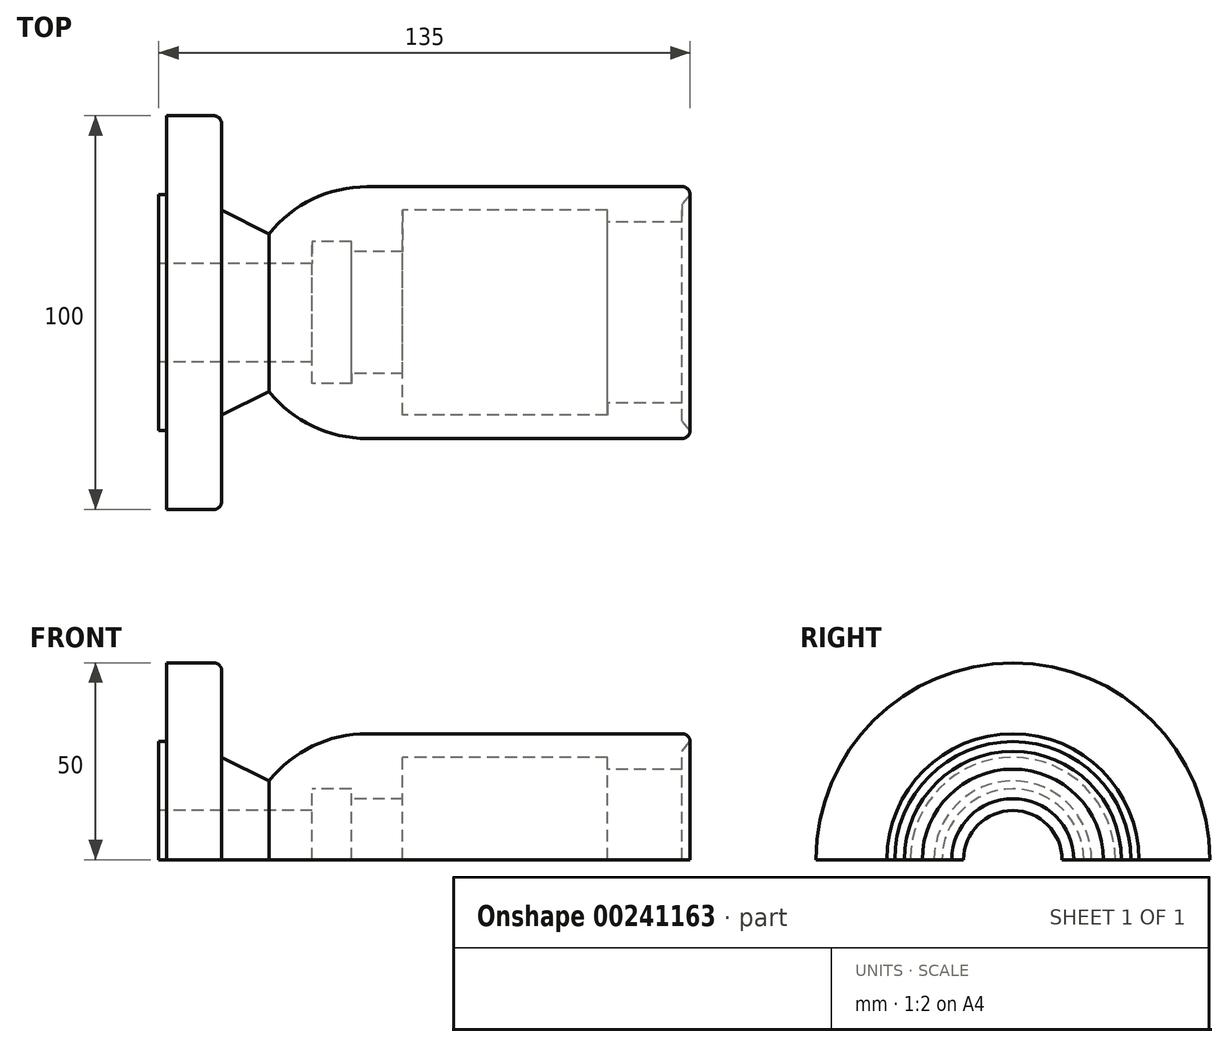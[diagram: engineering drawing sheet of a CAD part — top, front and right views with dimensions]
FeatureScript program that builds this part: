
annotation { "Feature Type Name" : "Feature", "Feature Type Description" : "" }
export const myFeature = defineFeature(function(context is Context, id is Id, definition is map)
    precondition{}
    {
        {
            var Q0;
            Q0=qCreatedBy(makeId("Front.planeOp"),FACE);
            var sketch = newSketch(context, id + "F0", { "sketchPlane" : qUnion([Q0])});
            skLineSegment(sketch, "E0", {"start": v(-75, 0) * mm, "end": v(60, 0) * mm});
            skLineSegment(sketch, "E1", {"start": v(60, 30) * mm, "end": v(60, -32) * mm});
            skLineSegment(sketch, "E2", {"start": v(-75, 30) * mm, "end": v(-75, -30) * mm});
            skLineSegment(sketch, "E3", {"start": v(-75, 30) * mm, "end": v(-73, 30) * mm});
            skLineSegment(sketch, "E4", {"start": v(-73, 30) * mm, "end": v(-73, 50) * mm});
            skLineSegment(sketch, "E5", {"start": v(-73, 50) * mm, "end": v(-61, 50) * mm});
            skLineSegment(sketch, "E6", {"start": v(58, 32) * mm, "end": v(-22.01, 32) * mm});
            skPoint(sketch, "E7.visualSharp", {"position": v(60, 32) * mm});
            skArc(sketch, "E7.filletArc", {"start": v(60, 30) * mm, "mid": v(59.42, 31.41) * mm, "end": v(58, 32) * mm});
            skLineSegment(sketch, "E8", {"start": v(60, 30) * mm, "end": v(58, 27.54) * mm});
            skLineSegment(sketch, "E9", {"start": v(58, 27.54) * mm, "end": v(58, 0) * mm});
            skLineSegment(sketch, "E10", {"start": v(58, 23) * mm, "end": v(39, 23) * mm});
            skLineSegment(sketch, "E11", {"start": v(39, 0) * mm, "end": v(39, 26) * mm});
            skLineSegment(sketch, "E12", {"start": v(39, 26) * mm, "end": v(-13, 26) * mm});
            skLineSegment(sketch, "E13", {"start": v(-13, 26) * mm, "end": v(-13, 0) * mm});
            skLineSegment(sketch, "E14", {"start": v(-13, 15.5) * mm, "end": v(-26, 15.5) * mm});
            skLineSegment(sketch, "E15", {"start": v(-26, 0) * mm, "end": v(-26, 18) * mm});
            skLineSegment(sketch, "E16", {"start": v(-26, 18) * mm, "end": v(-36, 18) * mm});
            skLineSegment(sketch, "E17", {"start": v(-36, 18) * mm, "end": v(-36, 0) * mm});
            skLineSegment(sketch, "E18", {"start": v(-36, 12.5) * mm, "end": v(-75, 12.5) * mm});
            skLineSegment(sketch, "E19", {"start": v(-59, 48) * mm, "end": v(-59, 26) * mm});
            skLineSegment(sketch, "E20", {"start": v(-59, 26) * mm, "end": v(-47, 20) * mm});
            skPoint(sketch, "E21.visualSharp", {"position": v(-59, 50) * mm});
            skArc(sketch, "E21.filletArc", {"start": v(-59, 48) * mm, "mid": v(-59.58, 49.41) * mm, "end": v(-61, 50) * mm});
            skArc(sketch, "E22", {"start": v(-22.01, 32) * mm, "mid": v(-35.87, 28.84) * mm, "end": v(-47, 20) * mm});
            skSolve(sketch);
        }
        {
            var Q0;
            {var subQ7=sQuery(id+"F0.wireOp",EDGE,"E3");Q0=makeQuery(id+"F0.imprint","IMPRINT",FACE,{"disambiguationData":[TD([[makeQuery(id+"F0.imprint","IMPRINT",EDGE,{"derivedFrom":subQ7}),-1.0]])]});}
            var Q1;
            Q1=sQuery(id+"F0.wireOp",EDGE,"E0");
            revolve(context, id + "F1", {"entities" : qUnion([Q0]), "axis" : qUnion([Q1]), "revolveType" : RevolveType.SYMMETRIC, "angle" : 180 * degree});
        }
    });
